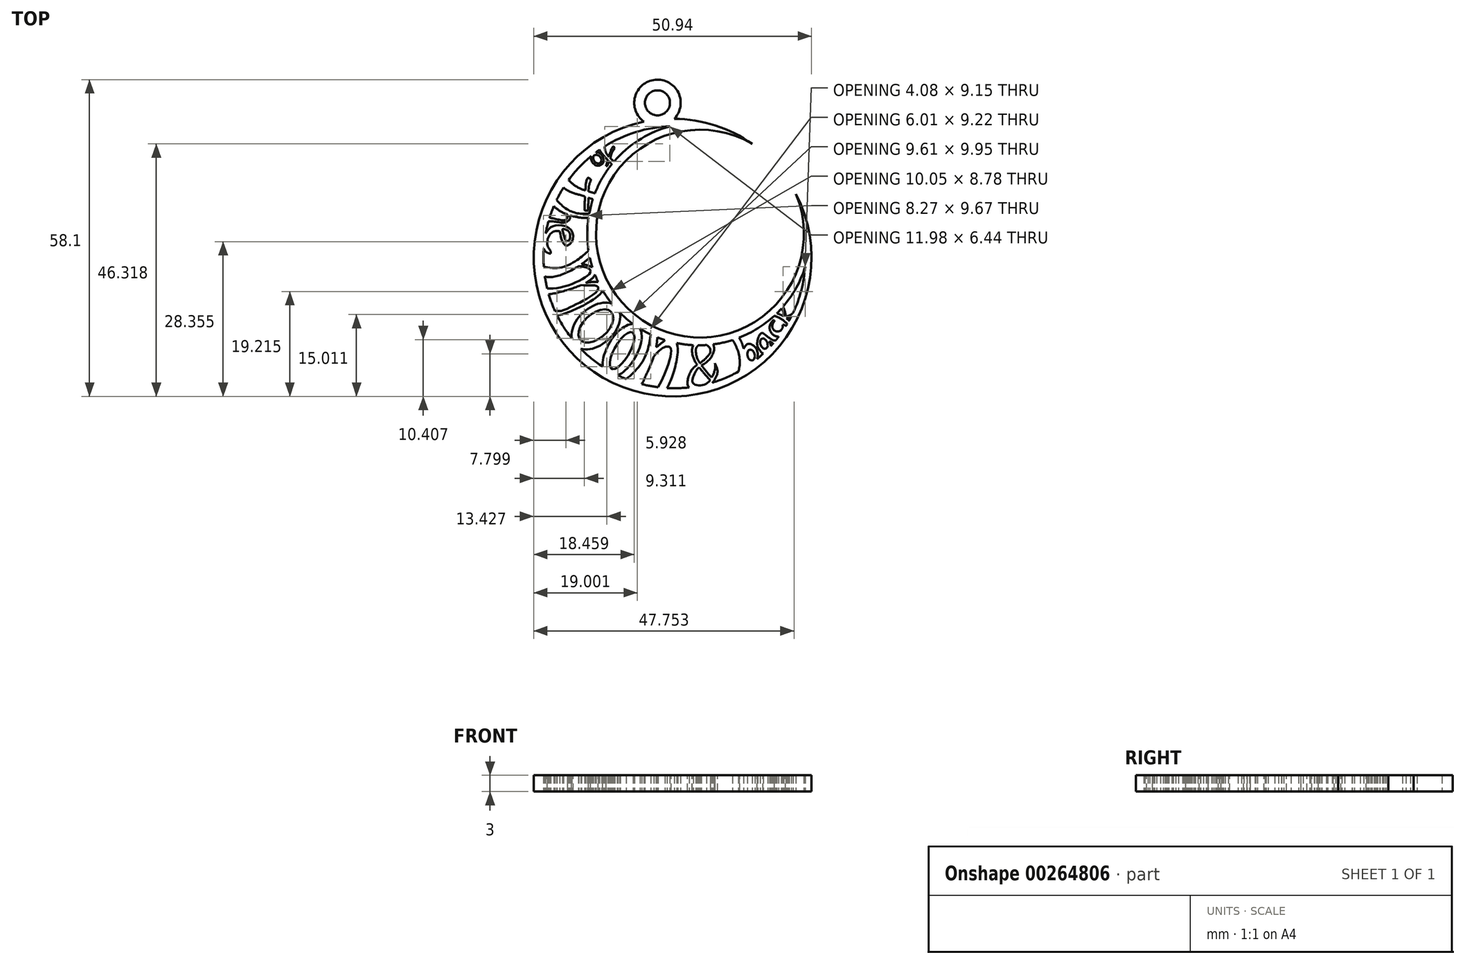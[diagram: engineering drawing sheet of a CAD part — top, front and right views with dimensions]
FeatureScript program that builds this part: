
annotation { "Feature Type Name" : "Feature", "Feature Type Description" : "" }
export const myFeature = defineFeature(function(context is Context, id is Id, definition is map)
    precondition{}
    {
        {
            var Q0;
            Q0=qCreatedBy(makeId("Top.planeOp"),FACE);
            var sketch = newSketch(context, id + "F0", { "sketchPlane" : qUnion([Q0])});
            skArc(sketch, "E0", {"start": v(9.59, 16.48) * mm, "mid": v(-24.2, -21.13) * mm, "end": v(17.62, 7.27) * mm});
            skArc(sketch, "E1", {"start": v(9.59, 16.48) * mm, "mid": v(-14.36, -12.54) * mm, "end": v(17.62, 7.27) * mm});
            skArc(sketch, "E2", {"start": v(-5.5, 19.69) * mm, "mid": v(-21.97, -21) * mm, "end": v(19.3, -6.06) * mm});
            skArc(sketch, "E3", {"start": v(-5.5, 19.69) * mm, "mid": v(-14.94, -14.23) * mm, "end": v(19.3, -6.06) * mm});
            skCircle(sketch, "E4", {"center": v(-7.79, 24) * mm, "radius": 4.26 * mm});
            skCircle(sketch, "E5", {"center": v(-7.79, 24) * mm, "radius": 2.3 * mm});
            skLineSegment(sketch, "E6", {"start": v(-5.5, 23.76) * mm, "end": v(-3.53, 23.76) * mm, "construction": true});
            skLineSegment(sketch, "E7", {"start": v(-20.28, 3.87) * mm, "end": v(-19.94, 5.33) * mm});
            skPoint(sketch, "E8.endSnap0", {"position": v(-17.2, 14.17) * mm});
            skLineSegment(sketch, "E9", {"start": v(-17.2, 11.3) * mm, "end": v(-16.74, 11.98) * mm});
            skLineSegment(sketch, "E10", {"start": v(-15.18, 13.87) * mm, "end": v(-15.62, 13.38) * mm});
            skSolve(sketch);
        }
        {
            var Q0;
            Q0=makeQuery(id+"F0.imprint","IMPRINT",FACE,{"disambiguationData":[TD([[makeQuery(id+"F0.imprint","IMPRINT",EDGE,{"derivedFrom":sQuery(id+"F0.wireOp",EDGE,"E5")}),-1.0]])]});
            var Q1;
            {var subQ0=sQuery(id+"F0.wireOp",EDGE,"E4");var subQ1=sQuery(id+"F0.wireOp",EDGE,"E0");var subQ2=makeQuery(id+"F0.imprint","INTERSECT",VERTEX,{"disambiguationData":[OD(0.0)],"derivedFrom":[subQ1,subQ0]});Q1=makeQuery(id+"F0.imprint","IMPRINT",FACE,{"disambiguationData":[TD([[makeQuery(id+"F0.imprint","IMPRINT",EDGE,{"disambiguationData":[TD([[subQ2,-1.0]])],"derivedFrom":subQ1}),1.0]])]});}
            var Q2;
            {var subQ9=sQuery(id+"F0.wireOp",EDGE,"E1");Q2=makeQuery(id+"F0.imprint","IMPRINT",FACE,{"disambiguationData":[TD([[makeQuery(id+"F0.imprint","IMPRINT",EDGE,{"derivedFrom":subQ9}),-1.0]])]});}
            extrude(context, id + "F1", {"entities" : qUnion([Q0, Q1, Q2]), "depth" : 3 * mm, "offsetDistance" : 25 * mm});
        }
        {
            var Q0;
            Q0=qCreatedBy(makeId("Top.planeOp"),FACE);
            var sketch = newSketch(context, id + "F2", { "sketchPlane" : qUnion([Q0])});
            skFitSpline(sketch, "E11", {"points": [v(-15.62, 13.16) * mm, v(-16.69, 14.1) * mm, v(-17.36, 15.23) * mm, v(-17.5, 16.77) * mm], "startDerivative": vector(-3.42, 2.68) * mm, "endDerivative": vector(0, 4.64) * mm});
            skFitSpline(sketch, "E12", {"points": [v(-17.5, 16.77) * mm, v(-18.5, 15.77) * mm, v(-16.69, 13.29) * mm, v(-15.62, 12.08) * mm], "startDerivative": vector(-5.36, -2.9) * mm, "endDerivative": vector(2.83, -3.39) * mm});
            skFitSpline(sketch, "E13", {"points": [v(-15.62, 12.08) * mm, v(-15.62, 13.16) * mm], "startDerivative": vector(0, 1.07) * mm, "endDerivative": vector(0, 1.07) * mm});
            skFitSpline(sketch, "E14", {"points": [v(-16.43, 13.83) * mm, v(-16.1, 14.96) * mm, v(-15.62, 15.65) * mm], "startDerivative": vector(0.5, 2.23) * mm, "endDerivative": vector(1.13, 1.37) * mm});
            skFitSpline(sketch, "E15", {"points": [v(-15.62, 15.65) * mm, v(-15.9, 15.98) * mm, v(-16.69, 14.1) * mm, v(-17.23, 12.42) * mm], "startDerivative": vector(-1.38, 2.8) * mm, "endDerivative": vector(-1.23, -3.7) * mm});
            skFitSpline(sketch, "E16", {"points": [v(-16.69, 13.29) * mm, v(-17.04, 12.42) * mm, v(-17.23, 12.42) * mm], "startDerivative": vector(-0.47, -1.69) * mm, "endDerivative": vector(-0.63, 0.2) * mm});
            skEllipse(sketch, "E17", {"center": v(-18.82, 13.68) * mm, "majorRadius": 1.29 * mm, "minorRadius": 1.1 * mm, "majorAxis": v(0.58, -0.81)});
            skEllipse(sketch, "E18", {"center": v(-18.82, 13.68) * mm, "majorRadius": 0.88 * mm, "minorRadius": 0.67 * mm, "majorAxis": v(0.62, -0.78)});
            skFitSpline(sketch, "E19", {"points": [v(-18.92, 7.32) * mm, v(-20.67, 7.82) * mm, v(-22.7, 8.67) * mm, v(-24.4, 10.2) * mm, v(-24.64, 10.87) * mm], "startDerivative": vector(-6.63, 1.88) * mm, "endDerivative": vector(-0.78, 3.8) * mm});
            skFitSpline(sketch, "E20", {"points": [v(-24.64, 10.87) * mm, v(-25.26, 8.9) * mm, v(-23.54, 7.57) * mm, v(-21.35, 6.9) * mm, v(-18.5, 6.16) * mm, v(-18.92, 7.32) * mm], "startDerivative": vector(-6.16, -10.57) * mm, "endDerivative": vector(-6.07, 9.87) * mm});
            skFitSpline(sketch, "E21", {"points": [v(-19.97, 9.88) * mm, v(-20.36, 8.7) * mm, v(-20.41, 7.75) * mm, v(-20.44, 6.58) * mm, v(-20.53, 4.25) * mm], "startDerivative": vector(-2.04, -5.1) * mm, "endDerivative": vector(-0.31, -7.76) * mm});
            skFitSpline(sketch, "E22", {"points": [v(-19.97, 9.88) * mm, v(-20.54, 10.22) * mm, v(-20.92, 9.17) * mm, v(-21, 7.92) * mm, v(-21.17, 4.5) * mm, v(-21.09, 4.24) * mm, v(-20.53, 4.25) * mm], "startDerivative": vector(-4.68, 4.64) * mm, "endDerivative": vector(5.58, 0.57) * mm});
            skFitSpline(sketch, "E23", {"points": [v(-19.32, 3.8) * mm, v(-21.8, 3.66) * mm, v(-24.65, 4.65) * mm, v(-26.76, 6.65) * mm, v(-27.14, 6.86) * mm], "startDerivative": vector(-8.7, -1.07) * mm, "endDerivative": vector(-2.89, 0.1) * mm});
            skFitSpline(sketch, "E24", {"points": [v(-27.14, 6.86) * mm, v(-27.14, 5.62) * mm, v(-24.83, 3.73) * mm, v(-20.8, 2.89) * mm, v(-19.17, 3.22) * mm], "startDerivative": vector(-1.46, -6.73) * mm, "endDerivative": vector(6.76, 2.25) * mm});
            skFitSpline(sketch, "E25", {"points": [v(-19.17, 3.22) * mm, v(-19.32, 3.8) * mm], "startDerivative": vector(-0.17, 0.68) * mm, "endDerivative": vector(-0.17, 0.68) * mm});
            skFitSpline(sketch, "E26", {"points": [v(-24.34, 3.53) * mm, v(-24.28, 2.96) * mm, v(-24.9, 2.45) * mm, v(-26.68, 2.76) * mm, v(-28.4, 2.9) * mm], "startDerivative": vector(1.03, -3.26) * mm, "endDerivative": vector(-5.47, 0.04) * mm});
            skFitSpline(sketch, "E27", {"points": [v(-23.79, 3.34) * mm, v(-23.86, 2.7) * mm, v(-24.79, 2.06) * mm, v(-26.53, 2.2) * mm, v(-27.92, 2.22) * mm, v(-28.7, 2.06) * mm], "startDerivative": vector(0.37, -4.2) * mm, "endDerivative": vector(-4.32, -1.16) * mm});
            skFitSpline(sketch, "E28", {"points": [v(-28.7, 2.06) * mm, v(-28.4, 2.9) * mm], "startDerivative": vector(0.3, 0.85) * mm, "endDerivative": vector(0.3, 0.85) * mm});
            skFitSpline(sketch, "E29", {"points": [v(-25.69, 0.42) * mm, v(-25.32, -1.19) * mm, v(-24.5, -2.2) * mm, v(-23.3, -0.99) * mm, v(-23.97, 0.98) * mm, v(-26.48, 1.52) * mm, v(-27.8, 0.76) * mm, v(-28.7, -1.16) * mm, v(-28.4, -3.19) * mm, v(-27.38, -3.67) * mm], "startDerivative": vector(2.37, -14.8) * mm, "endDerivative": vector(12.94, -2.8) * mm});
            skFitSpline(sketch, "E30", {"points": [v(-25.69, 0.42) * mm, v(-26.73, 0.42) * mm, v(-27.69, -0.42) * mm, v(-27.97, -2.03) * mm, v(-27.35, -3.19) * mm], "startDerivative": vector(-4.75, 0.7) * mm, "endDerivative": vector(3.17, -4.22) * mm});
            skFitSpline(sketch, "E31", {"points": [v(-27.35, -3.19) * mm, v(-27.38, -3.67) * mm], "startDerivative": vector(-0.03, -0.48) * mm, "endDerivative": vector(-0.03, -0.48) * mm});
            skFitSpline(sketch, "E32", {"points": [v(-25.14, 0.42) * mm, v(-24.84, -0.74) * mm, v(-24.38, -1.37) * mm, v(-23.9, -1.06) * mm, v(-23.8, -0.67) * mm, v(-23.82, -0.06) * mm, v(-24.35, 0.63) * mm, v(-25.17, 0.83) * mm, v(-25.14, 0.42) * mm]});
            skFitSpline(sketch, "E33", {"points": [v(-20.27, -2.95) * mm, v(-22.45, -4.8) * mm, v(-26.67, -6.34) * mm, v(-29.35, -6.14) * mm, v(-28.98, -7.51) * mm, v(-26.33, -7.81) * mm, v(-21.7, -5.6) * mm, v(-19.17, -3.36) * mm], "startDerivative": vector(-13.96, -13.4) * mm, "endDerivative": vector(13.92, 15.4) * mm});
            skFitSpline(sketch, "E34", {"points": [v(-19.17, -3.36) * mm, v(-20.27, -2.95) * mm], "startDerivative": vector(-0.94, 0.4) * mm, "endDerivative": vector(-0.94, 0.4) * mm});
            skFitSpline(sketch, "E35", {"points": [v(-21.7, -5.6) * mm, v(-20.86, -5.74) * mm, v(-20.05, -6.02) * mm, v(-19.17, -6.54) * mm, v(-19.17, -7.38) * mm, v(-20.26, -8.6) * mm, v(-24.54, -10.4) * mm, v(-28.34, -10.74) * mm], "startDerivative": vector(8.3, -1.16) * mm, "endDerivative": vector(4.5, 10.95) * mm});
            skFitSpline(sketch, "E36", {"points": [v(-22.23, -5.95) * mm, v(-21.08, -6.17) * mm, v(-20.27, -6.5) * mm, v(-20.08, -7.09) * mm, v(-21.77, -8.44) * mm, v(-26.48, -10.03) * mm, v(-28.6, -10.06) * mm, v(-28.34, -10.74) * mm], "startDerivative": vector(10.2, -1.77) * mm, "endDerivative": vector(8.83, -14.24) * mm});
            skFitSpline(sketch, "E37", {"points": [v(-20.94, -9.02) * mm, v(-19.5, -8.84) * mm, v(-18.24, -9.02) * mm, v(-17.7, -10.16) * mm, v(-20.7, -12.8) * mm, v(-23.48, -14.13) * mm, v(-25.62, -14.9) * mm, v(-26.98, -14.79) * mm, v(-27.35, -14.15) * mm, v(-26.11, -14.22) * mm, v(-23.8, -13.51) * mm, v(-20.9, -12.02) * mm, v(-18.75, -10.38) * mm, v(-18.77, -9.7) * mm, v(-19.91, -9.46) * mm, v(-21.83, -9.45) * mm], "startDerivative": vector(24.4, 3.6) * mm, "endDerivative": vector(-27.82, 1.12) * mm});
            skEllipse(sketch, "E38", {"center": v(-19.09, -16.95) * mm, "majorRadius": 5.2 * mm, "minorRadius": 3.4 * mm, "majorAxis": v(0.74, 0.67)});
            skEllipse(sketch, "E39", {"center": v(-19.09, -16.95) * mm, "majorRadius": 3.82 * mm, "minorRadius": 2.23 * mm, "majorAxis": v(0.74, 0.68)});
            skEllipse(sketch, "E40", {"center": v(-14.27, -21.44) * mm, "majorRadius": 5.4 * mm, "minorRadius": 2.72 * mm, "majorAxis": v(0.5, 0.87)});
            skEllipse(sketch, "E41", {"center": v(-14.27, -21.44) * mm, "majorRadius": 3.84 * mm, "minorRadius": 1.4 * mm, "majorAxis": v(0.5, 0.87)});
            skFitSpline(sketch, "E42", {"points": [v(-8.92, -17.54) * mm, v(-9.4, -20.62) * mm, v(-11, -24.17) * mm, v(-14.02, -27.06) * mm], "startDerivative": vector(-0.97, -9.88) * mm, "endDerivative": vector(-9.35, -7.53) * mm});
            skFitSpline(sketch, "E43", {"points": [v(-14.02, -27.06) * mm, v(-11.27, -28.06) * mm, v(-9.93, -26.05) * mm, v(-8.46, -22.5) * mm, v(-7.99, -18.07) * mm, v(-8.92, -17.54) * mm], "startDerivative": vector(15.15, -9.13) * mm, "endDerivative": vector(-9.04, 1.8) * mm});
            skFitSpline(sketch, "E44", {"points": [v(-8.04, -20.87) * mm, v(-6.91, -19.95) * mm, v(-5.7, -19.21) * mm, v(-4.3, -19.95) * mm, v(-5.04, -26.05) * mm, v(-6.58, -29.2) * mm], "startDerivative": vector(7.52, 5.93) * mm, "endDerivative": vector(-6.64, -10.95) * mm});
            skFitSpline(sketch, "E45", {"points": [v(-8.46, -22.5) * mm, v(-6.94, -21.05) * mm, v(-5.97, -20.72) * mm, v(-5.35, -21.05) * mm, v(-6.04, -24.67) * mm, v(-8, -28.84) * mm], "startDerivative": vector(7.37, 9.12) * mm, "endDerivative": vector(-7.14, -13.49) * mm});
            skFitSpline(sketch, "E46", {"points": [v(-8, -28.84) * mm, v(-6.58, -29.2) * mm], "startDerivative": vector(1.43, -0.36) * mm, "endDerivative": vector(1.43, -0.36) * mm});
            skFitSpline(sketch, "E47", {"points": [v(3.67, -27.2) * mm, v(0.9, -24.94) * mm, v(-0.56, -22.66) * mm, v(-0.75, -21.28) * mm, v(-0.67, -20.94) * mm], "startDerivative": vector(-9.59, 1.2) * mm, "endDerivative": vector(1.53, 6.37) * mm});
            skFitSpline(sketch, "E48", {"points": [v(-0.67, -20.94) * mm, v(0.28, -20.17) * mm, v(1.8, -20.94) * mm, v(1.78, -22.03) * mm, v(0.03, -23.8) * mm], "startDerivative": vector(3.64, 4.93) * mm, "endDerivative": vector(-9.2, -8) * mm});
            skFitSpline(sketch, "E49", {"points": [v(0.03, -23.8) * mm, v(-1.47, -24.94) * mm, v(-2.29, -27.43) * mm, v(-0.87, -28.69) * mm, v(1.54, -27.97) * mm, v(2.67, -26.8) * mm, v(3.43, -24.26) * mm], "startDerivative": vector(-6.76, -4.35) * mm, "endDerivative": vector(1.38, 13.69) * mm, "construction": true});
            skFitSpline(sketch, "E50", {"points": [v(3.67, -27.2) * mm, v(2.98, -27.63) * mm, v(0.38, -25.17) * mm, v(-1.13, -23) * mm, v(-1.4, -21.05) * mm, v(-0.55, -19.75) * mm, v(0.28, -19.45) * mm, v(1.79, -19.8) * mm, v(2.6, -21.13) * mm, v(1.47, -23.25) * mm, v(0.19, -24.02) * mm], "startDerivative": vector(-6.41, -14.22) * mm, "endDerivative": vector(-17.16, -11.3) * mm, "construction": true});
            skFitSpline(sketch, "E51", {"points": [v(3.43, -23.47) * mm, v(3.43, -24.26) * mm], "startDerivative": vector(0, -0.84) * mm, "endDerivative": vector(-0.14, -0.8) * mm});
            skFitSpline(sketch, "E52", {"points": [v(2.75, -23.78) * mm, v(3.22, -25.36) * mm, v(2.67, -26.8) * mm, v(1.38, -28.07) * mm, v(-1.67, -28.37) * mm, v(-2.29, -27.43) * mm, v(-1.47, -24.94) * mm, v(0.08, -23.74) * mm], "startDerivative": vector(5.44, -12.07) * mm, "endDerivative": vector(11.61, 6.27) * mm});
            skFitSpline(sketch, "E53", {"points": [v(-0.15, -24.52) * mm, v(-0.73, -25.18) * mm, v(-1.27, -26.4) * mm, v(-1.28, -27.4) * mm, v(0, -27.84) * mm, v(1.57, -27.2) * mm, v(2.67, -25.18) * mm, v(2.8, -24.2) * mm, v(2.75, -23.78) * mm], "startDerivative": vector(-6.38, -5.26) * mm, "endDerivative": vector(-1.03, 5.35) * mm});
            skFitSpline(sketch, "E54", {"points": [v(5.72, -19.04) * mm, v(6.95, -21.46) * mm, v(7.28, -24.11) * mm, v(6.85, -25.91) * mm], "startDerivative": vector(3.98, -6.52) * mm, "endDerivative": vector(-1.89, -5.76) * mm});
            skFitSpline(sketch, "E55", {"points": [v(6.85, -25.91) * mm, v(8.23, -25.25) * mm, v(8.28, -22.27) * mm, v(7.23, -19.18) * mm, v(6.24, -18.38) * mm], "startDerivative": vector(7.83, 1.68) * mm, "endDerivative": vector(-5.46, 3.09) * mm});
            skFitSpline(sketch, "E56", {"points": [v(6.24, -18.38) * mm, v(5.72, -19.04) * mm], "startDerivative": vector(-0.52, -0.66) * mm, "endDerivative": vector(-0.52, -0.66) * mm});
            skFitSpline(sketch, "E57", {"points": [v(8.02, -21.1) * mm, v(8.81, -20.23) * mm, v(10.1, -20.77) * mm, v(10.61, -22.27) * mm, v(10.14, -23.5) * mm, v(8.47, -24.47) * mm], "startDerivative": vector(3.72, 6.55) * mm, "endDerivative": vector(-8.41, -3.67) * mm});
            skEllipse(sketch, "E58", {"center": v(9.38, -22.27) * mm, "majorRadius": 1 * mm, "minorRadius": 0.68 * mm, "majorAxis": v(-0.24, 0.97)});
            skFitSpline(sketch, "E59", {"points": [v(11.05, -18.44) * mm, v(10.56, -19.69) * mm, v(10.66, -20.91) * mm, v(11.54, -22) * mm, v(11.81, -22) * mm, v(12.95, -21.01) * mm, v(12.86, -20.05) * mm, v(12.4, -19) * mm, v(11.58, -18.22) * mm, v(11.05, -18.44) * mm]});
            skEllipse(sketch, "E60", {"center": v(11.73, -20.18) * mm, "majorRadius": 0.98 * mm, "minorRadius": 0.64 * mm, "majorAxis": v(-0.33, 0.95)});
            skFitSpline(sketch, "E61", {"points": [v(11.58, -18.22) * mm, v(12.87, -19.24) * mm, v(13.83, -19.6) * mm, v(14.61, -19.58) * mm, v(13.87, -20.25) * mm, v(13.3, -20.06) * mm, v(12.75, -19.75) * mm], "startDerivative": vector(6.09, -4.97) * mm, "endDerivative": vector(-6.3, 3.6) * mm});
            skArc(sketch, "E62", {"start": v(13.55, -15.85) * mm, "mid": v(13.56, -18.65) * mm, "end": v(16.06, -17.39) * mm});
            skArc(sketch, "E63", {"start": v(13.78, -16.15) * mm, "mid": v(13.85, -17.87) * mm, "end": v(15.16, -16.75) * mm});
            skFitSpline(sketch, "E64", {"points": [v(15.16, -16.75) * mm, v(15.43, -16.75) * mm, v(15.88, -16.98) * mm, v(16.06, -17.39) * mm], "startDerivative": vector(0.9, 0.1) * mm, "endDerivative": vector(0.3, -1.26) * mm});
            skFitSpline(sketch, "E65", {"points": [v(13.55, -15.85) * mm, v(13.64, -16.04) * mm, v(13.47, -16.32) * mm, v(13.27, -16.98) * mm], "startDerivative": vector(0.82, -0.86) * mm, "endDerivative": vector(-0.13, -1.76) * mm});
            skFitSpline(sketch, "E66", {"points": [v(13.16, -14.9) * mm, v(14.22, -15.3) * mm, v(15.32, -15.94) * mm, v(16.5, -17.1) * mm], "startDerivative": vector(3.46, -1.19) * mm, "endDerivative": vector(3.1, -3.45) * mm});
            skFitSpline(sketch, "E67", {"points": [v(16.5, -17.1) * mm, v(16.8, -16.59) * mm, v(16.06, -15.69) * mm, v(14.89, -14.92) * mm, v(13.39, -14.54) * mm, v(13.16, -14.9) * mm], "startDerivative": vector(3.02, 3.09) * mm, "endDerivative": vector(-0.83, -3.5) * mm});
            skFitSpline(sketch, "E68", {"points": [v(15.37, -15.18) * mm, v(15.3, -14.49) * mm, v(15.24, -14.25) * mm, v(14.85, -13.63) * mm], "startDerivative": vector(-0.21, 2.1) * mm, "endDerivative": vector(-1.25, 1.8) * mm});
            skFitSpline(sketch, "E69", {"points": [v(14.85, -13.63) * mm, v(15.1, -13.33) * mm, v(15.61, -14.4) * mm, v(15.67, -15.38) * mm], "startDerivative": vector(1.03, 2.1) * mm, "endDerivative": vector(-0.16, -2.37) * mm});
            skFitSpline(sketch, "E70", {"points": [v(15.67, -15.38) * mm, v(16.3, -15.05) * mm, v(16.9, -14.7) * mm, v(17.63, -13.92) * mm], "startDerivative": vector(2.15, 0.82) * mm, "endDerivative": vector(2.06, 1.87) * mm, "construction": true});
            skFitSpline(sketch, "E71", {"points": [v(17.63, -13.92) * mm, v(17.63, -14.55) * mm, v(16.7, -15.22) * mm, v(15.9, -15.55) * mm, v(15.9, -15.55) * mm], "startDerivative": vector(0.55, -2.52) * mm, "endDerivative": vector(-0.17, 0.42) * mm, "construction": true});
            skFitSpline(sketch, "E72", {"points": [v(15.74, -15.2) * mm, v(16.2, -15.1) * mm], "startDerivative": vector(0.46, 0.1) * mm, "endDerivative": vector(0.46, 0.1) * mm});
            skFitSpline(sketch, "E73", {"points": [v(15.67, -14.7) * mm, v(15.74, -15.2) * mm], "startDerivative": vector(0.08, -0.5) * mm, "endDerivative": vector(0.08, -0.5) * mm});
            skLineSegment(sketch, "E74", {"start": v(17.27, -14.3) * mm, "end": v(17.32, -14.88) * mm});
            skFitSpline(sketch, "E75", {"points": [v(16.2, -15.1) * mm, v(16.55, -14.93) * mm, v(16.9, -14.7) * mm, v(17.27, -14.3) * mm], "startDerivative": vector(1.09, 0.58) * mm, "endDerivative": vector(1, 1.2) * mm});
            skFitSpline(sketch, "E76", {"points": [v(15.9, -15.55) * mm, v(16.7, -15.22) * mm, v(17.32, -14.88) * mm], "startDerivative": vector(1.6, 0.61) * mm, "endDerivative": vector(1.26, 0.74) * mm});
            skFitSpline(sketch, "E77", {"points": [v(3.67, -27.2) * mm, v(2.98, -27.63) * mm, v(0.38, -25.17) * mm, v(-0.15, -24.52) * mm, v(-1.1, -23.05) * mm, v(-1.4, -21.05) * mm, v(-0.55, -19.75) * mm, v(1.79, -19.8) * mm, v(2.6, -21.13) * mm, v(0.28, -24.15) * mm], "startDerivative": vector(-7.41, -10.42) * mm, "endDerivative": vector(-27.08, -10.75) * mm});
            skSolve(sketch);
        }
        {
            var Q0;
            {var subQ7=sQuery(id+"F2.wireOp",EDGE,"E13");Q0=makeQuery(id+"F2.imprint","IMPRINT",FACE,{"disambiguationData":[TD([[makeQuery(id+"F2.imprint","IMPRINT",EDGE,{"derivedFrom":subQ7}),1.0]])]});}
            var Q1;
            {var subQ0=sQuery(id+"F2.wireOp",EDGE,"E14");Q1=makeQuery(id+"F2.imprint","IMPRINT",FACE,{"disambiguationData":[TD([[makeQuery(id+"F2.imprint","IMPRINT",EDGE,{"derivedFrom":subQ0}),1.0]])]});}
            var Q2;
            {var subQ0=sQuery(id+"F2.wireOp",EDGE,"E12");var subQ1=sQuery(id+"F2.wireOp",EDGE,"E11");var subQ2=makeQuery(id+"F2.imprint","INTERSECT",VERTEX,{"derivedFrom":[subQ1,subQ0]});Q2=makeQuery(id+"F2.imprint","IMPRINT",FACE,{"disambiguationData":[TD([[makeQuery(id+"F2.imprint","IMPRINT",EDGE,{"disambiguationData":[TD([[subQ2,1.0]])],"derivedFrom":subQ1}),1.0]])]});}
            var Q3;
            {var subQ0=sQuery(id+"F2.wireOp",EDGE,"E16");Q3=makeQuery(id+"F2.imprint","IMPRINT",FACE,{"disambiguationData":[TD([[makeQuery(id+"F2.imprint","IMPRINT",EDGE,{"derivedFrom":subQ0}),-1.0]])]});}
            var Q4;
            Q4=makeQuery(id+"F2.imprint","IMPRINT",FACE,{"disambiguationData":[TD([[makeQuery(id+"F2.imprint","IMPRINT",EDGE,{"derivedFrom":sQuery(id+"F2.wireOp",EDGE,"E17")}),1.0]])]});
            var Q5;
            {var subQ0=sQuery(id+"F2.wireOp",EDGE,"E20");var subQ1=sQuery(id+"F2.wireOp",EDGE,"E19");var subQ2=makeQuery(id+"F2.imprint","INTERSECT",VERTEX,{"disambiguationData":[OD(0.0)],"derivedFrom":[subQ1,subQ0]});Q5=makeQuery(id+"F2.imprint","IMPRINT",FACE,{"disambiguationData":[TD([[makeQuery(id+"F2.imprint","IMPRINT",EDGE,{"disambiguationData":[TD([[subQ2,-1.0]])],"derivedFrom":subQ1}),1.0]])]});}
            var Q6;
            {var subQ0=sQuery(id+"F2.wireOp",EDGE,"E20");var subQ1=sQuery(id+"F2.wireOp",EDGE,"E19");var subQ2=makeQuery(id+"F2.imprint","INTERSECT",VERTEX,{"disambiguationData":[OD(1.0)],"derivedFrom":[subQ1,subQ0]});Q6=makeQuery(id+"F2.imprint","IMPRINT",FACE,{"disambiguationData":[TD([[makeQuery(id+"F2.imprint","IMPRINT",EDGE,{"disambiguationData":[TD([[subQ2,1.0]])],"derivedFrom":subQ1}),1.0]])]});}
            var Q7;
            {var subQ0=sQuery(id+"F2.wireOp",EDGE,"E21");var subQ1=sQuery(id+"F2.wireOp",EDGE,"E19");var subQ2=makeQuery(id+"F2.imprint","INTERSECT",VERTEX,{"derivedFrom":[subQ1,subQ0]});Q7=makeQuery(id+"F2.imprint","IMPRINT",FACE,{"disambiguationData":[TD([[makeQuery(id+"F2.imprint","IMPRINT",EDGE,{"disambiguationData":[TD([[subQ2,-1.0]])],"derivedFrom":subQ1}),1.0]])]});}
            var Q8;
            {var subQ0=sQuery(id+"F2.wireOp",EDGE,"E21");var subQ1=sQuery(id+"F2.wireOp",EDGE,"E19");var subQ2=makeQuery(id+"F2.imprint","INTERSECT",VERTEX,{"derivedFrom":[subQ1,subQ0]});Q8=makeQuery(id+"F2.imprint","IMPRINT",FACE,{"disambiguationData":[TD([[makeQuery(id+"F2.imprint","IMPRINT",EDGE,{"disambiguationData":[TD([[subQ2,-1.0]])],"derivedFrom":subQ1}),-1.0]])]});}
            var Q9;
            {var subQ0=sQuery(id+"F2.wireOp",EDGE,"E22");var subQ1=sQuery(id+"F2.wireOp",EDGE,"E20");var subQ2=makeQuery(id+"F2.imprint","INTERSECT",VERTEX,{"derivedFrom":[subQ1,subQ0]});Q9=makeQuery(id+"F2.imprint","IMPRINT",FACE,{"disambiguationData":[TD([[makeQuery(id+"F2.imprint","IMPRINT",EDGE,{"disambiguationData":[TD([[subQ2,-1.0]])],"derivedFrom":subQ1}),-1.0]])]});}
            var Q10;
            {var subQ4=sQuery(id+"F2.wireOp",EDGE,"E23");Q10=makeQuery(id+"F2.imprint","IMPRINT",FACE,{"disambiguationData":[TD([[makeQuery(id+"F2.imprint","IMPRINT",EDGE,{"derivedFrom":subQ4}),1.0]])]});}
            var Q11;
            {var subQ0=sQuery(id+"F2.wireOp",EDGE,"E26");Q11=makeQuery(id+"F2.imprint","IMPRINT",FACE,{"disambiguationData":[TD([[makeQuery(id+"F2.imprint","IMPRINT",EDGE,{"derivedFrom":subQ0}),1.0]])]});}
            var Q12;
            Q12=makeQuery(id+"F2.imprint","IMPRINT",FACE,{"disambiguationData":[TD([[makeQuery(id+"F2.imprint","IMPRINT",EDGE,{"derivedFrom":sQuery(id+"F2.wireOp",EDGE,"E29")}),1.0]])]});
            var Q13;
            {var subQ0=sQuery(id+"F2.wireOp",EDGE,"E34");Q13=makeQuery(id+"F2.imprint","IMPRINT",FACE,{"disambiguationData":[TD([[makeQuery(id+"F2.imprint","IMPRINT",EDGE,{"derivedFrom":subQ0}),1.0]])]});}
            var Q14;
            {var subQ6=sQuery(id+"F2.wireOp",EDGE,"E36");Q14=makeQuery(id+"F2.imprint","IMPRINT",FACE,{"disambiguationData":[TD([[makeQuery(id+"F2.imprint","IMPRINT",EDGE,{"derivedFrom":subQ6}),1.0]])]});}
            var Q15;
            {var subQ0=sQuery(id+"F2.wireOp",EDGE,"E37");Q15=makeQuery(id+"F2.imprint","IMPRINT",FACE,{"disambiguationData":[TD([[makeQuery(id+"F2.imprint","IMPRINT",EDGE,{"derivedFrom":subQ0}),-1.0]])]});}
            var Q16;
            Q16=makeQuery(id+"F2.imprint","IMPRINT",FACE,{"disambiguationData":[TD([[makeQuery(id+"F2.imprint","IMPRINT",EDGE,{"derivedFrom":sQuery(id+"F2.wireOp",EDGE,"E38")}),1.0]])]});
            var Q17;
            Q17=makeQuery(id+"F2.imprint","IMPRINT",FACE,{"disambiguationData":[TD([[makeQuery(id+"F2.imprint","IMPRINT",EDGE,{"derivedFrom":sQuery(id+"F2.wireOp",EDGE,"E40")}),1.0]])]});
            extrude(context, id + "F3", {"entities" : qUnion([Q0, Q1, Q2, Q3, Q4, Q5, Q6, Q7, Q8, Q9, Q10, Q11, Q12, Q13, Q14, Q15, Q16, Q17]), "operationType" : NewBodyOperationType.ADD, "depth" : 3 * mm, "offsetDistance" : 25 * mm});
        }
        {
            var Q0;
            {var subQ0=sQuery(id+"F2.wireOp",EDGE,"E42");Q0=makeQuery(id+"F2.imprint","IMPRINT",FACE,{"disambiguationData":[TD([[makeQuery(id+"F2.imprint","IMPRINT",EDGE,{"derivedFrom":subQ0}),1.0]])]});}
            var Q1;
            {var subQ0=sQuery(id+"F2.wireOp",EDGE,"E44");Q1=makeQuery(id+"F2.imprint","IMPRINT",FACE,{"disambiguationData":[TD([[makeQuery(id+"F2.imprint","IMPRINT",EDGE,{"derivedFrom":subQ0}),-1.0]])]});}
            var Q2;
            {var subQ1=sQuery(id+"F2.wireOp",EDGE,"E48");Q2=makeQuery(id+"F2.imprint","IMPRINT",FACE,{"disambiguationData":[TD([[makeQuery(id+"F2.imprint","IMPRINT",EDGE,{"derivedFrom":subQ1}),1.0]])]});}
            var Q3;
            {var subQ1=sQuery(id+"F2.wireOp",EDGE,"E47");var subQ3=sQuery(id+"F2.wireOp",EDGE,"E50");var subQ8=makeQuery(id+"F2.imprint","INTERSECT",VERTEX,{"disambiguationData":[OD(1.0)],"derivedFrom":[subQ1,subQ3]});Q3=makeQuery(id+"F2.imprint","IMPRINT",FACE,{"disambiguationData":[TD([[makeQuery(id+"F2.imprint","IMPRINT",EDGE,{"disambiguationData":[TD([[subQ8,1.0]])],"derivedFrom":subQ1}),1.0]])]});}
            var Q4;
            {var subQ0=sQuery(id+"F2.wireOp",EDGE,"E50");var subQ1=sQuery(id+"F2.wireOp",EDGE,"E47");var subQ2=makeQuery(id+"F2.imprint","INTERSECT",VERTEX,{"disambiguationData":[OD(1.0)],"derivedFrom":[subQ1,subQ0]});Q4=makeQuery(id+"F2.imprint","IMPRINT",FACE,{"disambiguationData":[TD([[makeQuery(id+"F2.imprint","IMPRINT",EDGE,{"disambiguationData":[TD([[subQ2,1.0]])],"derivedFrom":subQ1}),-1.0]])]});}
            var Q5;
            {var subQ0=sQuery(id+"F2.wireOp",EDGE,"E50");var subQ1=sQuery(id+"F2.wireOp",EDGE,"E49");var subQ2=makeQuery(id+"F2.imprint","INTERSECT",VERTEX,{"disambiguationData":[OD(0.0)],"derivedFrom":[subQ1,subQ0]});Q5=makeQuery(id+"F2.imprint","IMPRINT",FACE,{"disambiguationData":[TD([[makeQuery(id+"F2.imprint","IMPRINT",EDGE,{"disambiguationData":[TD([[subQ2,-1.0]])],"derivedFrom":subQ1}),1.0]])]});}
            var Q6;
            {var subQ0=sQuery(id+"F2.wireOp",EDGE,"ca650779-5d89-4ea1-bfbb-915ace64cc84");var subQ1=sQuery(id+"F2.wireOp",EDGE,"E47");var subQ2=makeQuery(id+"F2.imprint","INTERSECT",VERTEX,{"disambiguationData":[OD(0.0)],"derivedFrom":[subQ1,subQ0]});Q6=makeQuery(id+"F2.imprint","IMPRINT",FACE,{"disambiguationData":[TD([[makeQuery(id+"F2.imprint","IMPRINT",EDGE,{"disambiguationData":[TD([[subQ2,-1.0]])],"derivedFrom":subQ1}),1.0]])]});}
            var Q7;
            {var subQ5=sQuery(id+"F2.wireOp",EDGE,"E51");Q7=makeQuery(id+"F2.imprint","IMPRINT",FACE,{"disambiguationData":[TD([[makeQuery(id+"F2.imprint","IMPRINT",EDGE,{"derivedFrom":subQ5}),-1.0]])]});}
            var Q8;
            {var subQ0=sQuery(id+"F2.wireOp",EDGE,"E49");var subQ1=sQuery(id+"F2.wireOp",EDGE,"E47");var subQ2=makeQuery(id+"F2.imprint","INTERSECT",VERTEX,{"derivedFrom":[subQ1,subQ0]});Q8=makeQuery(id+"F2.imprint","IMPRINT",FACE,{"disambiguationData":[TD([[makeQuery(id+"F2.imprint","IMPRINT",EDGE,{"disambiguationData":[TD([[subQ2,-1.0]])],"derivedFrom":subQ1}),1.0]])]});}
            var Q9;
            {var subQ0=sQuery(id+"F2.wireOp",EDGE,"E50");var subQ1=sQuery(id+"F2.wireOp",EDGE,"E47");var subQ2=makeQuery(id+"F2.imprint","INTERSECT",VERTEX,{"disambiguationData":[OD(0.0)],"derivedFrom":[subQ1,subQ0]});Q9=makeQuery(id+"F2.imprint","IMPRINT",FACE,{"disambiguationData":[TD([[makeQuery(id+"F2.imprint","IMPRINT",EDGE,{"disambiguationData":[TD([[subQ2,-1.0]])],"derivedFrom":subQ1}),1.0]])]});}
            var Q10;
            {var subQ0=sQuery(id+"F2.wireOp",EDGE,"E52");var subQ1=sQuery(id+"F2.wireOp",EDGE,"E50");var subQ2=makeQuery(id+"F2.imprint","INTERSECT",VERTEX,{"disambiguationData":[OD(0.0)],"derivedFrom":[subQ1,subQ0]});Q10=makeQuery(id+"F2.imprint","IMPRINT",FACE,{"disambiguationData":[TD([[makeQuery(id+"F2.imprint","IMPRINT",EDGE,{"disambiguationData":[TD([[subQ2,-1.0]])],"derivedFrom":subQ1}),1.0]])]});}
            var Q11;
            {var subQ0=sQuery(id+"F2.wireOp",EDGE,"E52");var subQ1=sQuery(id+"F2.wireOp",EDGE,"E47");var subQ2=makeQuery(id+"F2.imprint","INTERSECT",VERTEX,{"disambiguationData":[OD(0.0)],"derivedFrom":[subQ1,subQ0]});Q11=makeQuery(id+"F2.imprint","IMPRINT",FACE,{"disambiguationData":[TD([[makeQuery(id+"F2.imprint","IMPRINT",EDGE,{"disambiguationData":[TD([[subQ2,-1.0]])],"derivedFrom":subQ1}),-1.0]])]});}
            var Q12;
            {var subQ0=sQuery(id+"F2.wireOp",EDGE,"E52");var subQ1=sQuery(id+"F2.wireOp",EDGE,"E47");var subQ2=makeQuery(id+"F2.imprint","INTERSECT",VERTEX,{"disambiguationData":[OD(0.0)],"derivedFrom":[subQ1,subQ0]});Q12=makeQuery(id+"F2.imprint","IMPRINT",FACE,{"disambiguationData":[TD([[makeQuery(id+"F2.imprint","IMPRINT",EDGE,{"disambiguationData":[TD([[subQ2,-1.0]])],"derivedFrom":subQ1}),1.0]])]});}
            var Q13;
            {var subQ5=sQuery(id+"F2.wireOp",EDGE,"E54");Q13=makeQuery(id+"F2.imprint","IMPRINT",FACE,{"disambiguationData":[TD([[makeQuery(id+"F2.imprint","IMPRINT",EDGE,{"derivedFrom":subQ5}),1.0]])]});}
            var Q14;
            {var subQ0=sQuery(id+"F2.wireOp",EDGE,"E57");Q14=makeQuery(id+"F2.imprint","IMPRINT",FACE,{"disambiguationData":[TD([[makeQuery(id+"F2.imprint","IMPRINT",EDGE,{"derivedFrom":subQ0}),-1.0]])]});}
            var Q15;
            Q15=makeQuery(id+"F2.imprint","IMPRINT",FACE,{"disambiguationData":[TD([[makeQuery(id+"F2.imprint","IMPRINT",EDGE,{"derivedFrom":sQuery(id+"F2.wireOp",EDGE,"E60")}),-1.0]])]});
            var Q16;
            {var subQ0=sQuery(id+"F2.wireOp",EDGE,"E61");var subQ1=sQuery(id+"F2.wireOp",EDGE,"E59");var subQ2=makeQuery(id+"F2.imprint","INTERSECT",VERTEX,{"disambiguationData":[OD(1.0)],"derivedFrom":[subQ1,subQ0]});Q16=makeQuery(id+"F2.imprint","IMPRINT",FACE,{"disambiguationData":[TD([[makeQuery(id+"F2.imprint","IMPRINT",EDGE,{"disambiguationData":[TD([[subQ2,-1.0]])],"derivedFrom":subQ1}),-1.0]])]});}
            extrude(context, id + "F4", {"entities" : qUnion([Q0, Q1, Q2, Q3, Q4, Q5, Q6, Q7, Q8, Q9, Q10, Q11, Q12, Q13, Q14, Q15, Q16]), "operationType" : NewBodyOperationType.ADD, "depth" : 3 * mm, "offsetDistance" : 25 * mm});
        }
        {
            var Q0;
            {var subQ5=sQuery(id+"F2.wireOp",EDGE,"E62");Q0=makeQuery(id+"F2.imprint","IMPRINT",FACE,{"disambiguationData":[TD([[makeQuery(id+"F2.imprint","IMPRINT",EDGE,{"derivedFrom":subQ5}),1.0]])]});}
            var Q1;
            {var subQ5=sQuery(id+"F2.wireOp",EDGE,"E66");Q1=makeQuery(id+"F2.imprint","IMPRINT",FACE,{"disambiguationData":[TD([[makeQuery(id+"F2.imprint","IMPRINT",EDGE,{"derivedFrom":subQ5}),1.0]])]});}
            extrude(context, id + "F5", {"entities" : qUnion([Q0, Q1]), "operationType" : NewBodyOperationType.ADD, "depth" : 3 * mm, "offsetDistance" : 25 * mm});
        }
        {
            var Q0;
            {var subQ0=sQuery(id+"F2.wireOp",EDGE,"E68");Q0=makeQuery(id+"F2.imprint","IMPRINT",FACE,{"disambiguationData":[TD([[makeQuery(id+"F2.imprint","IMPRINT",EDGE,{"derivedFrom":subQ0}),-1.0]])]});}
            var Q1;
            Q1=makeQuery(id+"F2.imprint","IMPRINT",FACE,{"disambiguationData":[TD([[makeQuery(id+"F2.imprint","IMPRINT",EDGE,{"derivedFrom":sQuery(id+"F2.wireOp",EDGE,"E72")}),-1.0]])]});
            var Q2;
            {var subQ0=sQuery(id+"F2.wireOp",EDGE,"E77");var subQ1=sQuery(id+"F2.wireOp",EDGE,"E52");var subQ2=makeQuery(id+"F2.imprint","INTERSECT",VERTEX,{"disambiguationData":[OD(0.0)],"derivedFrom":[subQ1,subQ0]});Q2=makeQuery(id+"F2.imprint","IMPRINT",FACE,{"disambiguationData":[TD([[makeQuery(id+"F2.imprint","IMPRINT",EDGE,{"disambiguationData":[TD([[subQ2,-1.0]])],"derivedFrom":subQ1}),-1.0]])]});}
            extrude(context, id + "F6", {"entities" : qUnion([Q0, Q1, Q2]), "operationType" : NewBodyOperationType.ADD, "depth" : 3 * mm, "offsetDistance" : 25 * mm});
        }
    });
